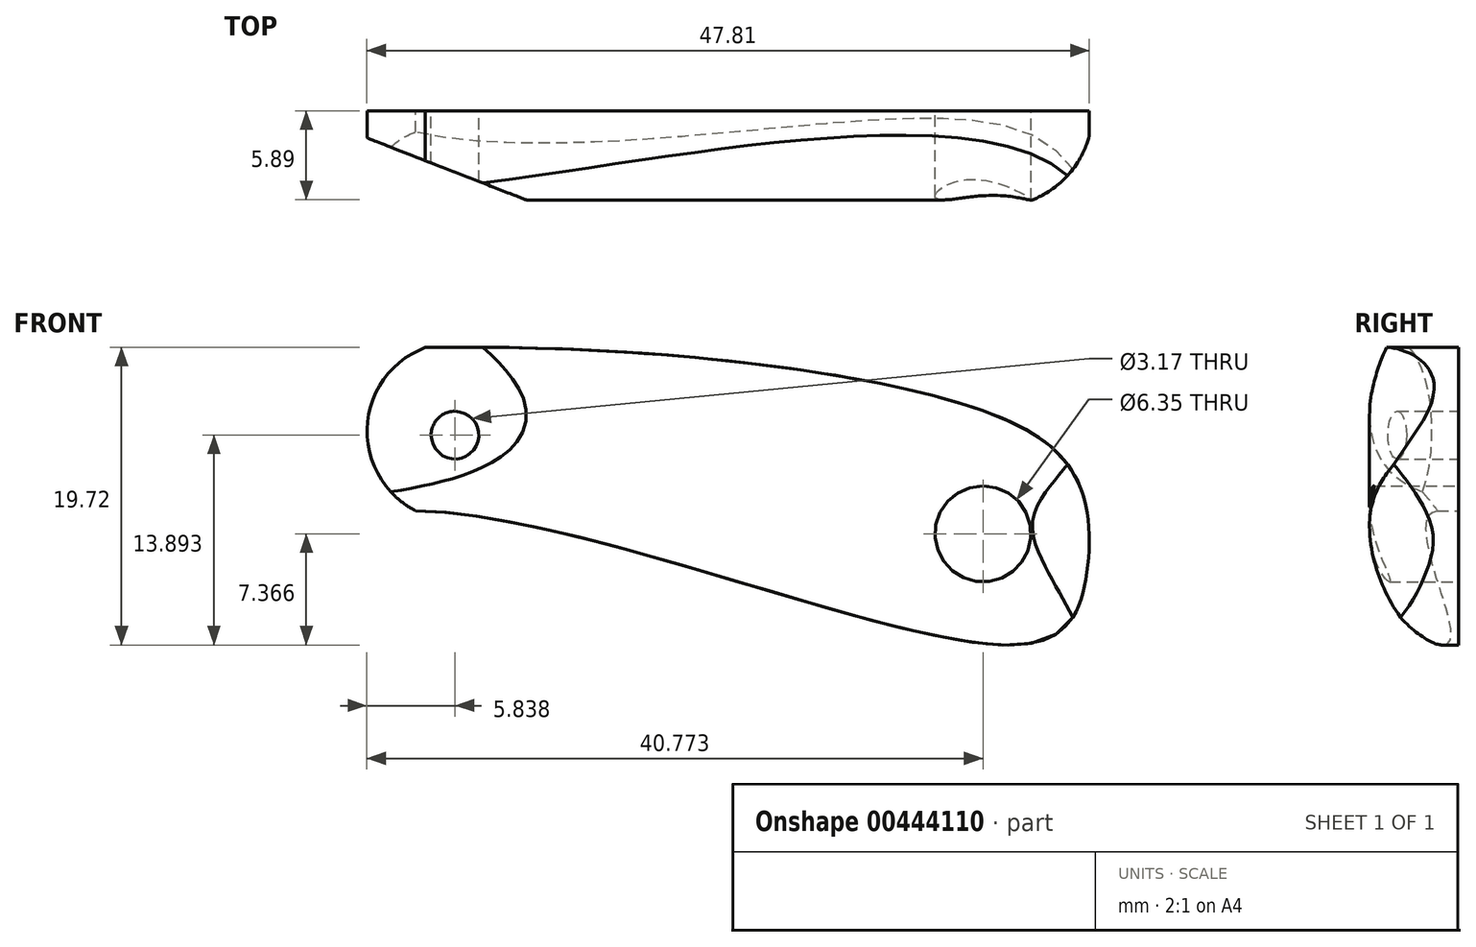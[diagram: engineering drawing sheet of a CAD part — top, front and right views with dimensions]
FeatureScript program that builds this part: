
annotation { "Feature Type Name" : "Feature", "Feature Type Description" : "" }
export const myFeature = defineFeature(function(context is Context, id is Id, definition is map)
    precondition{}
    {
        {
            var Q0;
            Q0=qCreatedBy(makeId("Front.planeOp"),FACE);
            var sketch = newSketch(context, id + "F0", { "sketchPlane" : qUnion([Q0])});
            skLineSegment(sketch, "E0", {"start": v(-1, 2.9) * mm, "end": v(0.18, 2.97) * mm});
            skPoint(sketch, "E1", {"position": v(48.62, 15.19) * mm});
            skPoint(sketch, "E2", {"position": v(13.69, 21.71) * mm});
            skArc(sketch, "E3", {"start": v(11.72, 27.52) * mm, "mid": v(7.86, 22.32) * mm, "end": v(11.07, 16.7) * mm});
            skFitSpline(sketch, "E4.trimOffspring", {"points": [v(-46.68, 0) * mm, v(-36.83, 14.74) * mm, v(0, 26.85) * mm, v(48.1, 23.51) * mm, v(54.92, 18.58) * mm, v(55.49, 12.52) * mm, v(51.4, 7.87) * mm, v(7.3, 16.37) * mm, v(0, 0) * mm], "startDerivative": vector(72.96, 165.42) * mm, "endDerivative": vector(-10.36, -190.7) * mm});
            skPoint(sketch, "E5.start.orphan", {"position": v(-1, 2.9) * mm});
            skPoint(sketch, "E6.start.orphan", {"position": v(-1.9, 17.09) * mm});
            skPoint(sketch, "E7.end.orphan", {"position": v(15.24, 75.7) * mm});
            skLineSegment(sketch, "E8", {"start": v(11.07, 16.7) * mm, "end": v(51.4, 7.87) * mm, "construction": true});
            skLineSegment(sketch, "E9", {"start": v(51.4, 7.87) * mm, "end": v(59.51, 44.88) * mm, "construction": true});
            skSolve(sketch);
        }
        {
            var Q0;
            Q0=makeQuery(id+"F0.imprint","IMPRINT",FACE,{"disambiguationData":[TD([[makeQuery(id+"F0.imprint","IMPRINT",EDGE,{"derivedFrom":sQuery(id+"F0.wireOp",EDGE,"E3")}),1.0]])]});
            extrude(context, id + "F1", {"entities" : qUnion([Q0]), "depth" : 6.35 * mm, "offsetDistance" : 25.4 * mm});
        }
        {
            var Q0;
            Q0=sQuery(id+"F0.wireOp",VERTEX,"E1");
            var Q1;
            Q1=makeQuery(id+"F1.opExtrude","SWEPT_BODY",BODY,{"disambiguationData":[OSD([sQuery(id+"F0.wireOp",EDGE,"E3"),sQuery(id+"F0.wireOp",EDGE,"E4.trimOffspring")])]});
            var Q2;
            Q2=makeQuery(id+"F1.opExtrude","SWEPT_BODY",BODY,{"disambiguationData":[OSD([sQuery(id+"F0.wireOp",EDGE,"E3"),sQuery(id+"F0.wireOp",EDGE,"E4.trimOffspring")])]});
            hole(context, id + "F2", {"style" : HoleStyle.SIMPLE, "endStyle" : HoleEndStyle.THROUGH, "oppositeDirection" : true, "holeDiameter" : 6.35 * mm, "isTappedThrough" : true, "tappedDepth" : 12.7 * mm, "tapClearance" : 3, "locations" : qUnion([Q0]), "scope" : qUnion([Q1, Q2])});
        }
        {
            var Q0;
            Q0=sQuery(id+"F0.wireOp",VERTEX,"E2");
            var Q1;
            Q1=makeQuery(id+"F1.opExtrude","SWEPT_BODY",BODY,{"disambiguationData":[OSD([sQuery(id+"F0.wireOp",EDGE,"E3"),sQuery(id+"F0.wireOp",EDGE,"E4.trimOffspring")])]});
            hole(context, id + "F3", {"style" : HoleStyle.SIMPLE, "endStyle" : HoleEndStyle.THROUGH, "oppositeDirection" : true, "holeDiameter" : 3.17 * mm, "isTappedThrough" : true, "tappedDepth" : 12.7 * mm, "tapClearance" : 3, "locations" : qUnion([Q0]), "scope" : qUnion([Q1])});
        }
        {
            var Q0;
            Q0=sQuery(id+"F0.wireOp",EDGE,"E9");
            var Q1;
            Q1=qCreatedBy(makeId("Right.planeOp"),FACE);
            cPlane(context, id + "F4", {"entities" : qUnion([Q0, Q1]), "cplaneType" : CPlaneType.LINE_ANGLE, "offset" : 25.4 * mm, "angle" : 0 * degree, "width" : 152.4 * mm, "height" : 152.4 * mm});
        }
        {
            var Q0;
            Q0=qCreatedBy(id+"F4.planeOp",FACE);
            var sketch = newSketch(context, id + "F5", { "sketchPlane" : qUnion([Q0])});
            skLineSegment(sketch, "E10", {"start": v(0, 14.17) * mm, "end": v(0, 44.65) * mm});
            skLineSegment(sketch, "E11.bottom", {"start": v(-13.26, 16.68) * mm, "end": v(13.26, 16.68) * mm});
            skLineSegment(sketch, "E11.top", {"start": v(-13.26, 37.07) * mm, "end": v(13.26, 37.07) * mm});
            skLineSegment(sketch, "E11.left", {"start": v(-13.26, 16.68) * mm, "end": v(-13.26, 37.07) * mm});
            skLineSegment(sketch, "E11.right", {"start": v(13.26, 16.68) * mm, "end": v(13.26, 37.07) * mm});
            skPoint(sketch, "E11.middle", {"position": v(0, 26.87) * mm});
            skPoint(sketch, "E12", {"position": v(0, 9.1) * mm});
            skLineSegment(sketch, "E13", {"start": v(0, 14.17) * mm, "end": v(0, 9.1) * mm});
            skLineSegment(sketch, "E14.top", {"start": v(13.26, 10.15) * mm, "end": v(-13.26, 10.15) * mm});
            skLineSegment(sketch, "E14.left", {"start": v(13.26, 16.68) * mm, "end": v(13.26, 10.15) * mm});
            skLineSegment(sketch, "E14.right", {"start": v(-13.26, 16.68) * mm, "end": v(-13.26, 10.15) * mm});
            skFitSpline(sketch, "E15", {"points": [v(0, 34.75) * mm, v(4.18, 31.05) * mm, v(5.88, 26.87) * mm, v(4.57, 22.12) * mm, v(0, 17.61) * mm], "startDerivative": vector(18.03, -13.57) * mm, "endDerivative": vector(-19.34, -14.01) * mm});
            skSolve(sketch);
        }
        {
            var Q0;
            {var subQ0=sQuery(id+"F5.wireOp",EDGE,"E11.right");Q0=makeQuery(id+"F5.imprint","IMPRINT",FACE,{"disambiguationData":[TD([[makeQuery(id+"F5.imprint","IMPRINT",EDGE,{"derivedFrom":subQ0}),1.0]])]});}
            extrude(context, id + "F6", {"entities" : qUnion([Q0]), "operationType" : NewBodyOperationType.REMOVE, "endBound" : BoundingType.SYMMETRIC, "depth" : 127 * mm, "offsetDistance" : 25.4 * mm});
        }
        {
            var Q0;
            Q0=qCreatedBy(makeId("Top.planeOp"),FACE);
            var sketch = newSketch(context, id + "F7", { "sketchPlane" : qUnion([Q0])});
            skLineSegment(sketch, "E16", {"start": v(3.25, 0) * mm, "end": v(22.75, -7.58) * mm});
            skLineSegment(sketch, "E17", {"start": v(0, 0) * mm, "end": v(30.44, 0) * mm});
            skLineSegment(sketch, "E18.MirrorCS", {"start": v(3.25, 0) * mm, "end": v(22.75, 7.58) * mm});
            skLineSegment(sketch, "E19.bottom", {"start": v(0, -11.84) * mm, "end": v(16.71, -11.84) * mm});
            skLineSegment(sketch, "E19.top", {"start": v(0, 10.52) * mm, "end": v(16.71, 10.52) * mm});
            skLineSegment(sketch, "E19.left", {"start": v(0, -11.84) * mm, "end": v(0, 10.52) * mm});
            skLineSegment(sketch, "E20", {"start": v(16.71, 10.52) * mm, "end": v(21.9, 10.52) * mm});
            skLineSegment(sketch, "E21", {"start": v(21.9, 10.52) * mm, "end": v(22.39, -11.84) * mm});
            skLineSegment(sketch, "E22", {"start": v(22.39, -11.84) * mm, "end": v(16.71, -11.84) * mm});
            skCircle(sketch, "E23", {"center": v(49.53, 0) * mm, "radius": 6.35 * mm});
            skLineSegment(sketch, "E24.bottom", {"start": v(49.53, 0) * mm, "end": v(59.2, 0) * mm});
            skLineSegment(sketch, "E24.top", {"start": v(49.53, -9.67) * mm, "end": v(59.2, -9.67) * mm});
            skLineSegment(sketch, "E24.left", {"start": v(49.53, 0) * mm, "end": v(49.53, -9.67) * mm});
            skLineSegment(sketch, "E24.right", {"start": v(59.2, 0) * mm, "end": v(59.2, -9.67) * mm});
            skSolve(sketch);
        }
        {
            var Q0;
            {var subQ0=sQuery(id+"F7.wireOp",EDGE,"E19.bottom");Q0=makeQuery(id+"F7.imprint","IMPRINT",FACE,{"disambiguationData":[TD([[makeQuery(id+"F7.imprint","IMPRINT",EDGE,{"derivedFrom":subQ0}),1.0]])]});}
            var Q1;
            {var subQ0=sQuery(id+"F7.wireOp",EDGE,"E24.top");Q1=makeQuery(id+"F7.imprint","IMPRINT",FACE,{"disambiguationData":[TD([[makeQuery(id+"F7.imprint","IMPRINT",EDGE,{"derivedFrom":subQ0}),1.0]])]});}
            extrude(context, id + "F8", {"entities" : qUnion([Q0, Q1]), "operationType" : NewBodyOperationType.REMOVE, "endBound" : BoundingType.SYMMETRIC, "oppositeDirection" : true, "depth" : 76.2 * mm, "offsetDistance" : 25.4 * mm});
        }
    });
